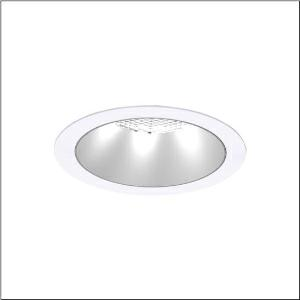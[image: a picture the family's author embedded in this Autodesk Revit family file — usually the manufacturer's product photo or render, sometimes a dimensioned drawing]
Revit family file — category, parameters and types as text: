
# Revit family: lunis_21_xl_51db19mf91c
name_source: partatom
category: Lighting Fixtures
units: mm (PartAtom-declared; Revit-internal decimal feet)

## family parameters
Cut with Voids When Loaded = No
Host = Face
Light Source = No
Part Type = Normal
Room Calculation Point = No
Round Connector Dimension = Use Diameter
Shared = No

## types (1)
- --- (1 x LED, 3590 lm, 21.7 W, 4000K)
    Apparent Load = 22 VA
    CIE Flux Codes = 95 98 100 100 100
    Color Rendering = 80
    Color Temperature = 4000K
    Default Elevation = 1800 mm
    Description = Lunis 21,  XL, downlight, light control with lens, of PMMA, anti glare with reflector, of PC, matt, light emission: direct distribution, LED rated luminous flux: 2.390lm, light colour: 830/840/865, with terminal, 3-pole, mains connection: 220..240V, AC/DC, 0/50..60Hz, housing, round, of diecast aluminium, traffic white (RAL 9016), diameter: 230mm, clamping range: 1..40mm, protection rating (complete): IP20, protection rating (on room side): IP54, insulation class (complete): insulation class II (safety insulation), certification: CE, impact resistance: IK03, packaging unit: 1 piece
    Height = 0 mm  [stored 0 ft]
    Lamp = 1 x LED
    Lamp Light Flux = 3590 lm
    Lamp Power = 21.7 W
    Lamp count = 1
    Length = 230 mm
    Luminous efficacy = 165 lm/W
    Manufacturer = Siteco
    ModVariant = No
    Model = 51DB19MF91C
    Mounting Place = Ceiling
    Mounting Type = Recessed
    Number of Poles = 1
    OnlyDefault = Yes
    Power Factor = 1
    Product Name = Lunis 21 XL
    Product group = downlight
    ProductGroupID = 400
    Protection Class = Protection class II
    Protection Degree = IP 20
    RLX_Detail_Level = 1
    RLX_Emergency_Light_Flux = 0 lm
    RLX_Emergency_Type = 0
    RLX_Emergency_Type_DB = No
    RlxData = <blob elided: 18701 chars, md5=f06ce217>
    Socket = socket
    Standby Power = 0 W
    System Light Flux = 3590 lm
    System Power = 22 W
    Type Comments = individual setting: colour temperature 4000K, luminous flux: 100 % | (OFF | ON | ON | ON) | 650 mA
    Type Image = l_1291163.jpg
    URL = http://relux.com
    VarID = @adj_019103
    Voltage = 0 V
    Weight = 0.00 kg
    Width = 0 mm  [stored 0 ft]

note: [stored X ft] marks values corroborated as IEEE doubles in the binary element streams (Revit-internal decimal feet)

## geometry (parser evidence)
native form markers: Blend x4, Sweep x11
no freeform markers — native parametric forms only
